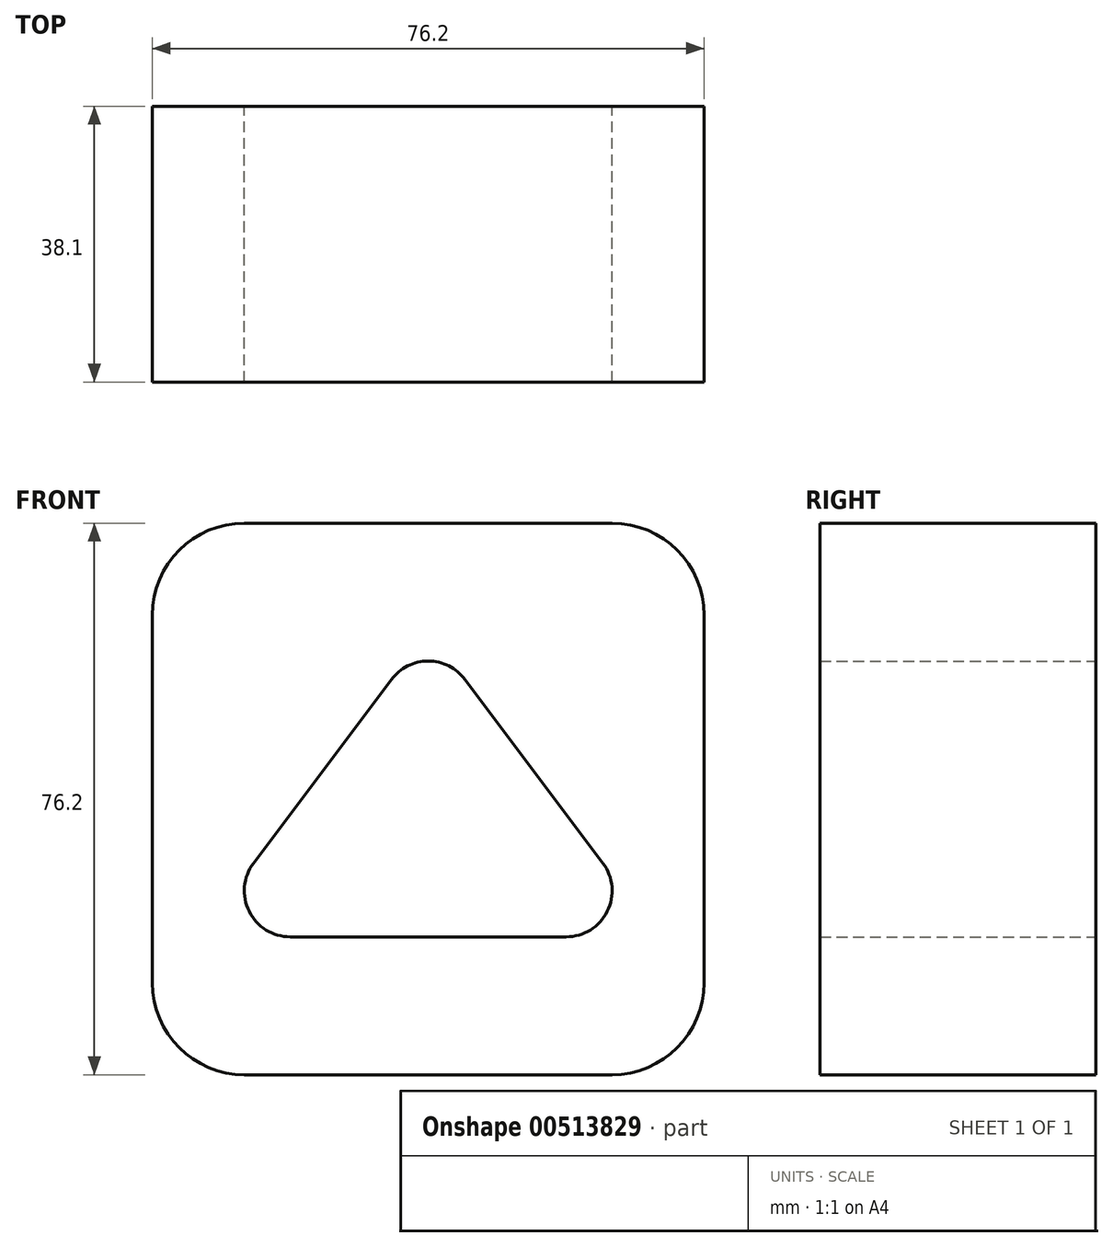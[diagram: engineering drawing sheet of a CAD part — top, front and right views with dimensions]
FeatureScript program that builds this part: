
annotation { "Feature Type Name" : "Feature", "Feature Type Description" : "" }
export const myFeature = defineFeature(function(context is Context, id is Id, definition is map)
    precondition{}
    {
        {
            var Q0;
            Q0=qCreatedBy(makeId("Front.planeOp"),FACE);
            var sketch = newSketch(context, id + "F0", { "sketchPlane" : qUnion([Q0])});
            skLineSegment(sketch, "E0", {"start": v(12.7, 0) * mm, "end": v(63.5, 0) * mm});
            skLineSegment(sketch, "E1", {"start": v(76.2, 12.7) * mm, "end": v(76.2, 63.5) * mm});
            skLineSegment(sketch, "E2", {"start": v(63.5, 76.2) * mm, "end": v(12.7, 76.2) * mm});
            skLineSegment(sketch, "E3", {"start": v(0, 63.5) * mm, "end": v(0, 12.7) * mm});
            skPoint(sketch, "E4.visualSharp", {"position": v(0, 76.2) * mm});
            skArc(sketch, "E4.filletArc", {"start": v(12.7, 76.2) * mm, "mid": v(3.72, 72.48) * mm, "end": v(0, 63.5) * mm});
            skPoint(sketch, "E5.visualSharp", {"position": v(76.2, 76.2) * mm});
            skArc(sketch, "E5.filletArc", {"start": v(76.2, 63.5) * mm, "mid": v(72.48, 72.48) * mm, "end": v(63.5, 76.2) * mm});
            skArc(sketch, "E6", {"start": v(13.97, 29.21) * mm, "mid": v(13.37, 22.56) * mm, "end": v(19.05, 19.05) * mm});
            skArc(sketch, "E7", {"start": v(57.15, 19.05) * mm, "mid": v(62.83, 22.56) * mm, "end": v(62.23, 29.21) * mm});
            skArc(sketch, "E8", {"start": v(43.18, 54.6) * mm, "mid": v(38.1, 57.15) * mm, "end": v(33.02, 54.6) * mm});
            skLineSegment(sketch, "E9", {"start": v(33.02, 54.6) * mm, "end": v(13.97, 29.21) * mm});
            skLineSegment(sketch, "E10", {"start": v(19.05, 19.05) * mm, "end": v(57.15, 19.05) * mm});
            skLineSegment(sketch, "E11", {"start": v(62.23, 29.21) * mm, "end": v(43.18, 54.6) * mm});
            skArc(sketch, "E12", {"start": v(0, 12.7) * mm, "mid": v(3.72, 3.72) * mm, "end": v(12.7, 0) * mm});
            skPoint(sketch, "E13.orphan", {"position": v(0, 0) * mm});
            skArc(sketch, "E14", {"start": v(63.5, 0) * mm, "mid": v(72.48, 3.72) * mm, "end": v(76.2, 12.7) * mm});
            skPoint(sketch, "E15.orphan", {"position": v(76.2, 0) * mm});
            skSolve(sketch);
        }
        {
            var Q0;
            Q0=makeQuery(id+"F0.imprint","IMPRINT",FACE,{"disambiguationData":[TD([[makeQuery(id+"F0.imprint","IMPRINT",EDGE,{"derivedFrom":sQuery(id+"F0.wireOp",EDGE,"E0")}),1.0]])]});
            extrude(context, id + "F1", {"entities" : qUnion([Q0]), "depth" : 38.1 * mm, "offsetDistance" : 25.4 * mm});
        }
    });
